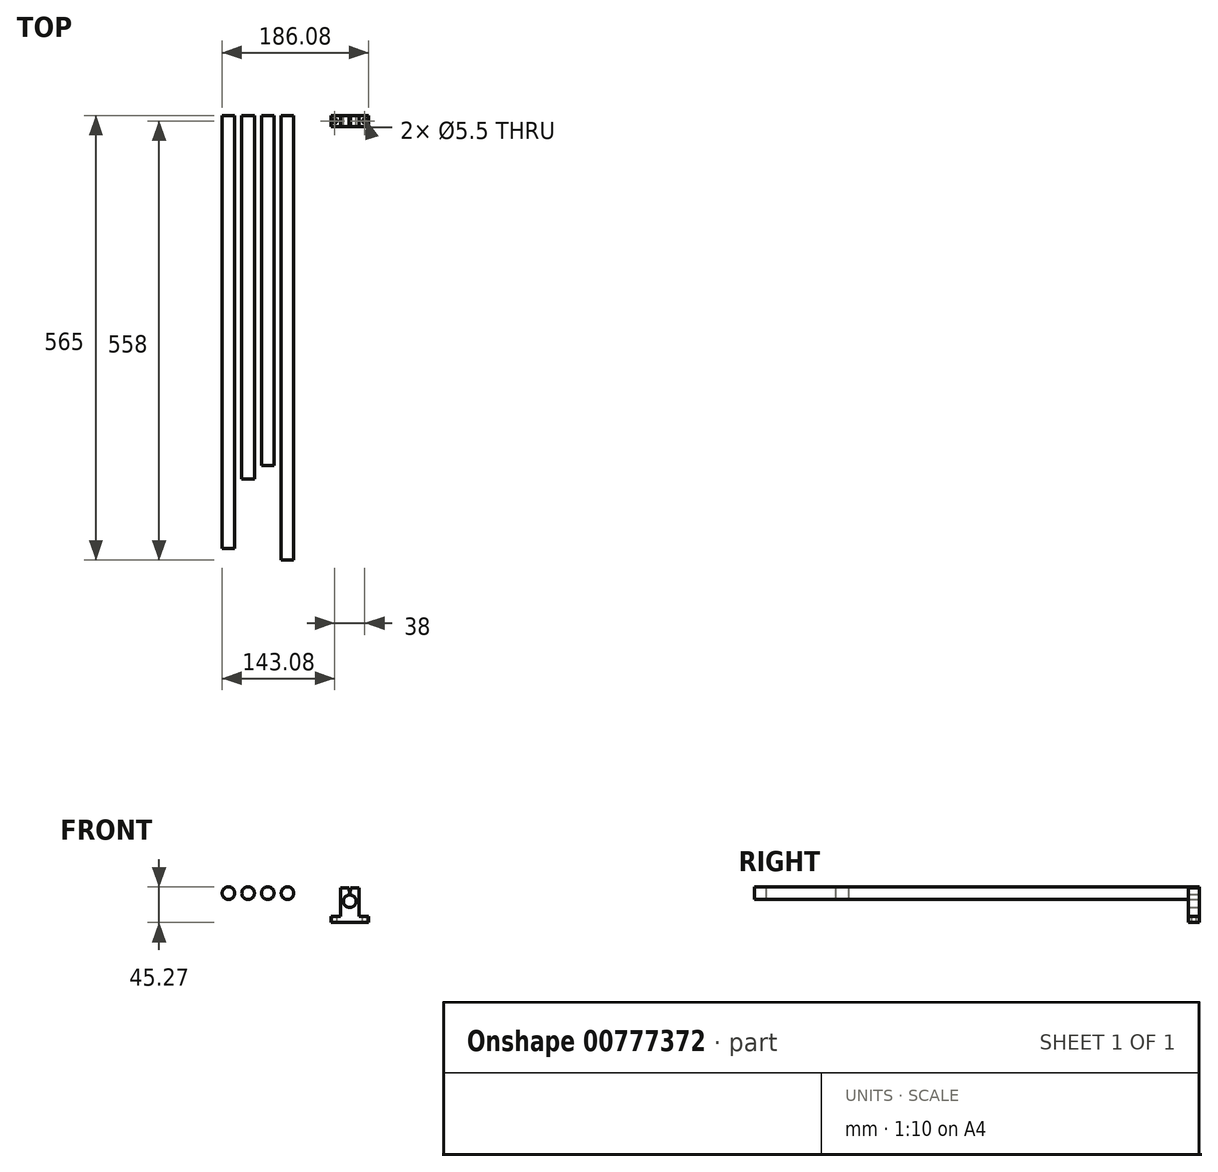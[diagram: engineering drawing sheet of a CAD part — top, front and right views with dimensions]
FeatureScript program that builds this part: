
annotation { "Feature Type Name" : "Feature", "Feature Type Description" : "" }
export const myFeature = defineFeature(function(context is Context, id is Id, definition is map)
    precondition{}
    {
        {
            var Q0;
            Q0=qCreatedBy(makeId("Front.planeOp"),FACE);
            var sketch = newSketch(context, id + "F0", { "sketchPlane" : qUnion([Q0])});
            skLineSegment(sketch, "E0", {"start": v(-24, 0) * mm, "end": v(-24, 8) * mm});
            skLineSegment(sketch, "E1", {"start": v(-24, 8) * mm, "end": v(-12, 8) * mm});
            skLineSegment(sketch, "E2", {"start": v(-12, 8) * mm, "end": v(-12, 44) * mm});
            skLineSegment(sketch, "E3", {"start": v(-12, 44) * mm, "end": v(0, 44) * mm});
            skLineSegment(sketch, "E4", {"start": v(-24, 0) * mm, "end": v(0, 0) * mm});
            skArc(sketch, "E5", {"start": v(0, 35) * mm, "mid": v(-8, 27) * mm, "end": v(0, 19) * mm});
            skLineSegment(sketch, "E6.trimOffspring", {"start": v(0, 35) * mm, "end": v(0, 44) * mm});
            skLineSegment(sketch, "E7", {"start": v(0, 0) * mm, "end": v(0, 19) * mm});
            skSolve(sketch);
        }
        {
            var Q0;
            Q0=makeQuery(id+"F0.imprint","IMPRINT",FACE,{"disambiguationData":[TD([[makeQuery(id+"F0.imprint","IMPRINT",EDGE,{"derivedFrom":sQuery(id+"F0.wireOp",EDGE,"E0")}),-1.0]])]});
            extrude(context, id + "F1", {"entities" : qUnion([Q0]), "depth" : 14 * mm, "offsetDistance" : 25 * mm});
        }
        {
            var Q0;
            Q0=makeQuery(id+"F1.opExtrude","SWEPT_FACE",FACE,{"disambiguationData":[OSD([sQuery(id+"F0.wireOp",EDGE,"E1")])]});
            var sketch = newSketch(context, id + "F2", { "sketchPlane" : qUnion([Q0])});
            skLineSegment(sketch, "E8.0.0", {"start": v(-12, 0) * mm, "end": v(-24, 0) * mm});
            skLineSegment(sketch, "E8.0.1", {"start": v(-24, 0) * mm, "end": v(-24, -14) * mm});
            skLineSegment(sketch, "E8.0.2", {"start": v(-24, -14) * mm, "end": v(-12, -14) * mm});
            skLineSegment(sketch, "E8.0.3", {"start": v(-12, -14) * mm, "end": v(-12, 0) * mm});
            skCircle(sketch, "E9", {"center": v(-19, -7) * mm, "radius": 2.75 * mm});
            skPoint(sketch, "E9.centerSnap0", {"position": v(-24, -7) * mm});
            skPoint(sketch, "E9.centerSnap1", {"position": v(-18, 0) * mm});
            skSolve(sketch);
        }
        {
            var Q0;
            Q0=makeQuery(id+"F2.imprint","IMPRINT",FACE,{"disambiguationData":[TD([[makeQuery(id+"F2.imprint","IMPRINT",EDGE,{"derivedFrom":sQuery(id+"F2.wireOp",EDGE,"E9")}),1.0]])]});
            extrude(context, id + "F3", {"entities" : qUnion([Q0]), "operationType" : NewBodyOperationType.REMOVE, "oppositeDirection" : true, "depth" : 25 * mm, "offsetDistance" : 25 * mm});
        }
        {
            var Q0;
            Q0=makeQuery(id+"F1.opExtrude","CAP_FACE",FACE,{"disambiguationData":[OSD([sQuery(id+"F0.wireOp",EDGE,"E0"),sQuery(id+"F0.wireOp",EDGE,"E1"),sQuery(id+"F0.wireOp",EDGE,"E2"),sQuery(id+"F0.wireOp",EDGE,"E3"),sQuery(id+"F0.wireOp",EDGE,"E4"),sQuery(id+"F0.wireOp",EDGE,"E5"),sQuery(id+"F0.wireOp",EDGE,"E6.trimOffspring"),sQuery(id+"F0.wireOp",EDGE,"E7")])],"isStart":false});
            var sketch = newSketch(context, id + "F4", { "sketchPlane" : qUnion([Q0])});
            skLineSegment(sketch, "E10", {"start": v(-0.8, 44) * mm, "end": v(-0.5, 34.98) * mm});
            skSolve(sketch);
        }
        {
            var Q0;
            {var subQ0=sQuery(id+"F4.wireOp",EDGE,"E10");Q0=makeQuery(id+"F4.imprint","IMPRINT",FACE,{"disambiguationData":[TD([[makeQuery(id+"F4.imprint","IMPRINT",EDGE,{"derivedFrom":subQ0}),1.0]])]});}
            extrude(context, id + "F5", {"entities" : qUnion([Q0]), "operationType" : NewBodyOperationType.REMOVE, "oppositeDirection" : true, "depth" : 25 * mm, "offsetDistance" : 25 * mm});
        }
        {
            var Q0;
            Q0=makeQuery(id+"F1.opExtrude","SWEPT_BODY",BODY,{"disambiguationData":[OSD([sQuery(id+"F0.wireOp",EDGE,"E0"),sQuery(id+"F0.wireOp",EDGE,"E1"),sQuery(id+"F0.wireOp",EDGE,"E2"),sQuery(id+"F0.wireOp",EDGE,"E3"),sQuery(id+"F0.wireOp",EDGE,"E4"),sQuery(id+"F0.wireOp",EDGE,"E5"),sQuery(id+"F0.wireOp",EDGE,"E6.trimOffspring"),sQuery(id+"F0.wireOp",EDGE,"E7")])]});
            var Q1;
            Q1=makeQuery(id+"F1.opExtrude","SWEPT_FACE",FACE,{"disambiguationData":[OSD([sQuery(id+"F0.wireOp",EDGE,"E7")])]});
            mirror(context, id + "F6", {"operationType" : NewBodyOperationType.ADD, "entities" : qUnion([Q0]), "mirrorPlane" : qUnion([Q1])});
        }
        {
            var Q0;
            Q0=qCreatedBy(makeId("Front.planeOp"),FACE);
            var sketch = newSketch(context, id + "F7", { "sketchPlane" : qUnion([Q0])});
            skCircle(sketch, "E11", {"center": v(-154.08, 37.27) * mm, "radius": 8 * mm});
            skCircle(sketch, "E12.1.0.0", {"center": v(-129.08, 37.27) * mm, "radius": 8 * mm});
            skCircle(sketch, "E12.2.0.0", {"center": v(-104.08, 37.27) * mm, "radius": 8 * mm});
            skLineSegment(sketch, "E12.direction1", {"start": v(-154.08, 37.27) * mm, "end": v(-129.08, 37.27) * mm, "construction": true});
            skCircle(sketch, "E13.0.3.0", {"center": v(-79.08, 37.27) * mm, "radius": 8 * mm});
            skSolve(sketch);
        }
        {
            var Q0;
            Q0=makeQuery(id+"F7.imprint","IMPRINT",FACE,{"disambiguationData":[TD([[makeQuery(id+"F7.imprint","IMPRINT",EDGE,{"derivedFrom":sQuery(id+"F7.wireOp",EDGE,"E11")}),1.0]])]});
            extrude(context, id + "F8", {"entities" : qUnion([Q0]), "depth" : 550 * mm, "offsetDistance" : 25 * mm});
        }
        {
            var Q0;
            Q0=makeQuery(id+"F7.imprint","IMPRINT",FACE,{"disambiguationData":[TD([[makeQuery(id+"F7.imprint","IMPRINT",EDGE,{"derivedFrom":sQuery(id+"F7.wireOp",EDGE,"E12.1.0.0")}),1.0]])]});
            extrude(context, id + "F9", {"entities" : qUnion([Q0]), "depth" : 462 * mm, "offsetDistance" : 25 * mm});
        }
        {
            var Q0;
            Q0=makeQuery(id+"F7.imprint","IMPRINT",FACE,{"disambiguationData":[TD([[makeQuery(id+"F7.imprint","IMPRINT",EDGE,{"derivedFrom":sQuery(id+"F7.wireOp",EDGE,"E12.2.0.0")}),1.0]])]});
            extrude(context, id + "F10", {"entities" : qUnion([Q0]), "depth" : 445 * mm, "offsetDistance" : 25 * mm});
        }
        {
            var Q0;
            Q0=makeQuery(id+"F7.imprint","IMPRINT",FACE,{"disambiguationData":[TD([[makeQuery(id+"F7.imprint","IMPRINT",EDGE,{"derivedFrom":sQuery(id+"F7.wireOp",EDGE,"E13.0.3.0")}),1.0]])]});
            extrude(context, id + "F11", {"entities" : qUnion([Q0]), "depth" : 565 * mm, "offsetDistance" : 25 * mm});
        }
    });
